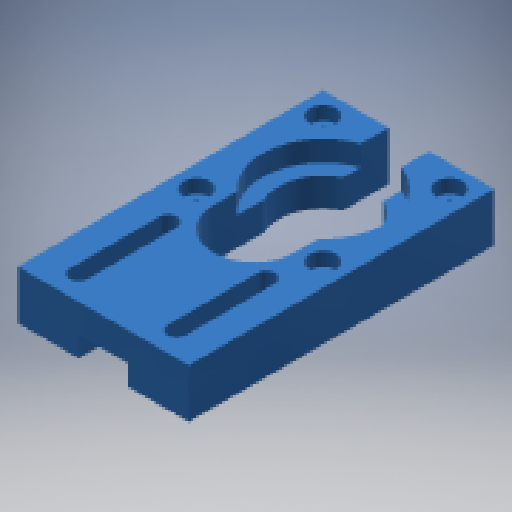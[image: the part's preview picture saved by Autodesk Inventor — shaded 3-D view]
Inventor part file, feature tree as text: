
AUTODESK INVENTOR PART (.ipt)
format: ipt  version: 2024.3 (Build 283343000, 343)  size: 383,488 bytes
history: native  units: mm
features: projected_geometry x8, extrude x7, sketch x7, hole x1
ambient origin geometry x8: Origin, YZ Plane, XZ Plane, XY Plane, X Axis, Y Axis, Z Axis, Center Point
bodies: Volumenkörper1 (feature_tree)
feature tree (23):
  extrude  "Extrusion1"  Depth=75.0mm
  hole  "Bohrung1"  [1 undecoded]
  extrude  "Extrusion2"  Depth=31.0mm
  extrude  "Extrusion3"  Depth=24.0mm
  extrude  "Extrusion4"  Depth=8.0mm
  extrude  "Extrusion5"  Depth=22.0mm
  extrude  "Extrusion6"  Depth=5.0mm TaperAngle=0.0deg
  extrude  "Extrusion7"  Depth=4.4mm
  sketch  "Skizze2"  dims[d0=42.0mm d1=75.0mm]
  projected_geometry  "Projizierte Kontur1"
  sketch  "Skizze3"  dims[d3=22.0mm d4=21.0mm]
  projected_geometry  "Projizierte Kontur2"
  sketch  "Skizze4"  dims[d5=12.0mm d6=0.0mm d7=31.0mm]
  projected_geometry  "Projizierte Kontur3"
  projected_geometry  "Projizierte Kontur4"
  sketch  "Skizze5"  dims[d8=31.0mm]
  projected_geometry  "Projizierte Kontur5"
  sketch  "Skizze6"  dims[d9=3.4mm d10=6.0mm d11=6.5mm d12=3.4mm d13=90.0deg d14=8.0mm d15=20.594885mm d16=24.0mm]
  projected_geometry  "Projizierte Kontur6"
  sketch  "Skizze7"  dims[d17=8.0mm d18=8.0mm]
  projected_geometry  "Projizierte Kontur7"
  sketch  "Skizze8"  dims[d19=6.0mm d20=22.0mm d21=5.0mm d22=0.0mm d23=4.4mm d24=4.4mm d25=0.0mm d26=0.0mm d27=30.0mm d28=5.0mm d29=0.0mm d30=18.0mm d31=10.0mm d32=8.0mm d33=0.0mm d34=0.0mm d35=20.0mm d36=17.0mm d37=10.0mm d38=0.0mm d39=12.0mm d40=60.0mm d41=5.0mm d42=0.0mm]
  projected_geometry  "Projizierte Kontur8"
note: 1 required parameter value undecoded (feature->parameter linkage not recoverable at this tier; creation-order binding heuristic only, values carry confidence <= 0.55)
